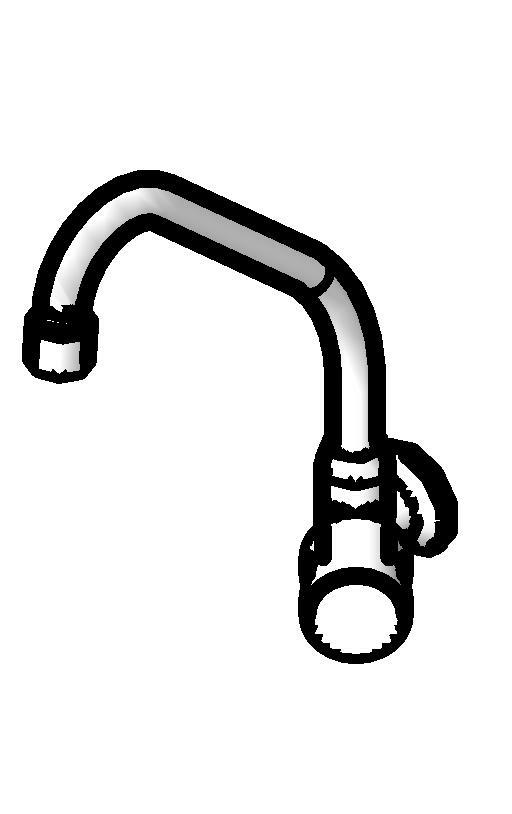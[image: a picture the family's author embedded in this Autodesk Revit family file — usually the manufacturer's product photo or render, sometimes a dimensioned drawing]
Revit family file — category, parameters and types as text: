
# Revit family: Deca_Torneira de parede para cozinha_Aspen_1168.35
name_source: partatom
category: Plumbing Fixtures
units: mm (PartAtom-declared; Revit-internal decimal feet)

## family parameters
Cut with Voids When Loaded = No
Host = Face
Part Type = Normal
Room Calculation Point = No
Round Connector Dimension = Use Radius
Shared = No

## types (1)
- 1168.C35_Cromado
    Acompanha o Produto = -
    Aprovado por = quattroD
    Atendimento ao Cliente = 0800-0117073
    CWFU = 0
    Categoria = METAIS PARA COZINHA
    Composição Anel Vedação = -
    Composição Assento = -
    Composição Básica = Liga de Cobre (bronze e latão),Plásticos de Engenharia,Elastômeros
    Composição Componente = -
    Consumo = -
    Cor Interna = -
    Cor Principal = Cromado
    Cor Secundária = -
    Cores Componente = -
    Criado por = quattroD
    Código Pai = 1168.35
    Default Elevation = 110 mm  [stored 0.360892 ft]
    Description = Torneira de parede para cozinha
    Diâmetro Água Fria = 15 mm  [stored 0.0492126 ft]
    HWFU = 0
    Informações Complementares = -
    Itens de Instalação = -
    Linha = Aspen
    Manufacturer = Deca
    Material = Deca_Cromado
    Model = 1168.C35
    Norma = NBR10281
    Peso Líquido (Kg) = 0.675
    Pressão máx. funcionamento = 40 MCA
    Pressão mín. Aquec. Acúmulo = -
    Pressão mín. Aquec. Passagem = -
    Pressão mín. funcionamento = 2 MCA
    Raio Água Fria = 8 mm  [stored 0.0262467 ft]
    Saída de Esgoto = -
    Segmento = Banheiro Competitivo
    Tipo de dispositivo economizador = Não
    Tipo de mecanismo utilizado = MVC -1/4 volta
    Tipo de rosca de entrada = BSP NBR 8133
    Tipo de rosca de saída = -
    URL = www.deca.com.br
    Vazão na Pressão máx. (L/min) = 16
    Vazão na Pressão mín. (L/min) = 4

note: source unit labels omitted for Vazão na Pressão máx. (L/min), Vazão na Pressão mín. (L/min) — the stored unit's dimension contradicts the parameter name (converter mislabeling)

note: [stored X ft] marks values corroborated as IEEE doubles in the binary element streams (Revit-internal decimal feet)

## geometry (parser evidence)
native form markers: Sweep x3
no freeform markers — native parametric forms only
